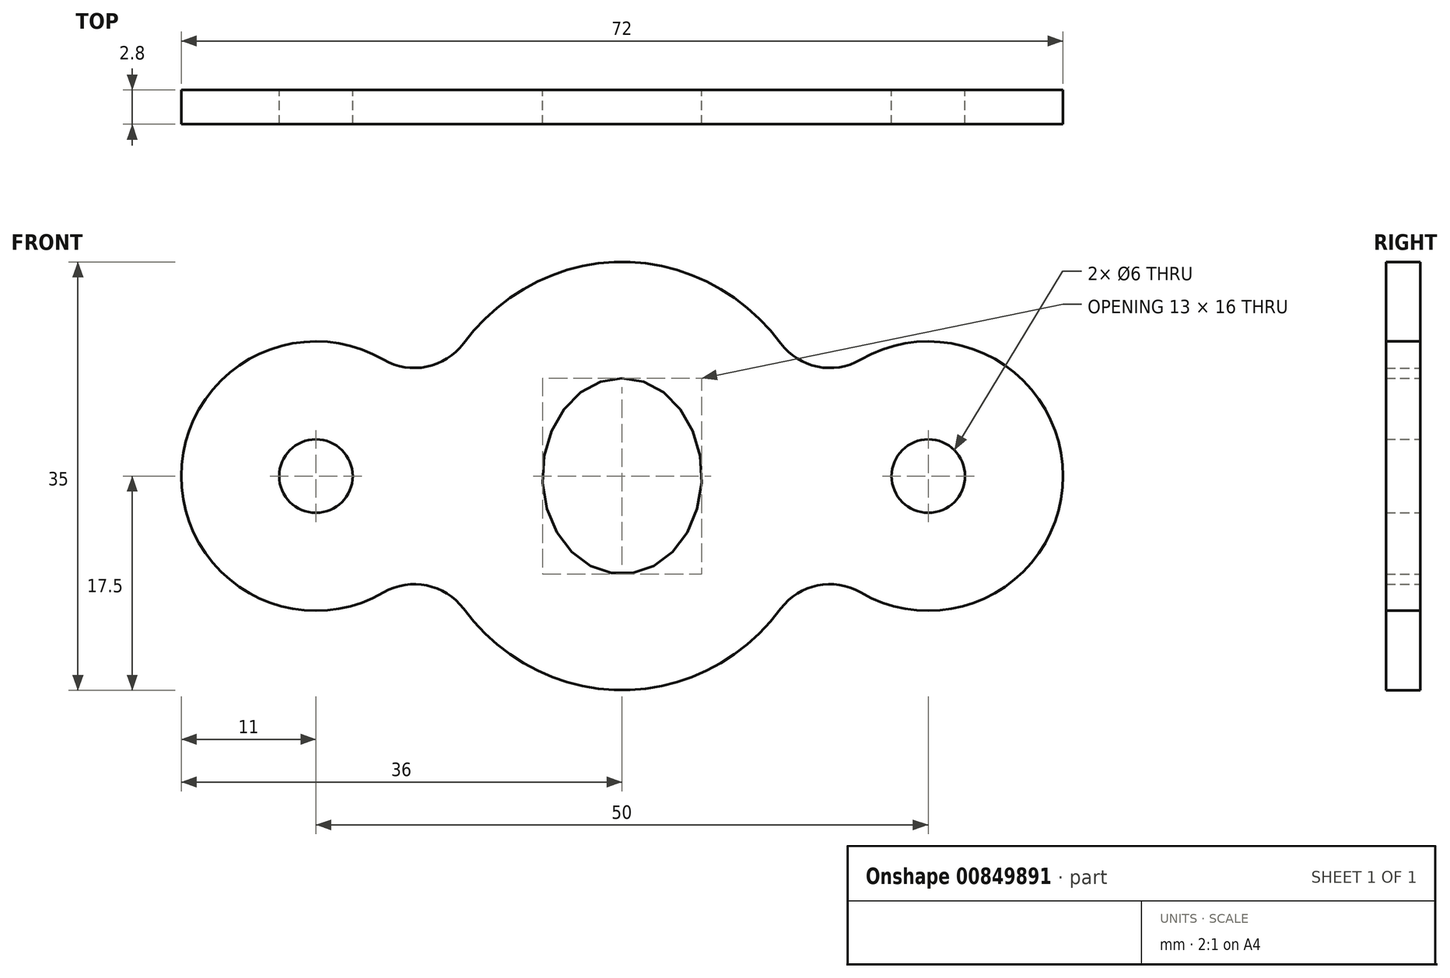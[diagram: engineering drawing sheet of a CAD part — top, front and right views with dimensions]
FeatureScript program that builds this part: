
annotation { "Feature Type Name" : "Feature", "Feature Type Description" : "" }
export const myFeature = defineFeature(function(context is Context, id is Id, definition is map)
    precondition{}
    {
        {
            var Q0;
            Q0=qCreatedBy(makeId("Front.planeOp"),FACE);
            var sketch = newSketch(context, id + "F0", { "sketchPlane" : qUnion([Q0])});
            skEllipse(sketch, "E0", {"center": v(0, 0) * mm, "majorRadius": 17.5 * mm, "minorRadius": 16.5 * mm, "majorAxis": v(0, 1)});
            skCircle(sketch, "E1", {"center": v(25, 0) * mm, "radius": 11 * mm});
            skCircle(sketch, "E2", {"center": v(-25, 0) * mm, "radius": 11 * mm});
            skCircle(sketch, "E3", {"center": v(-25, 0) * mm, "radius": 3 * mm});
            skCircle(sketch, "E4", {"center": v(25, 0) * mm, "radius": 3 * mm});
            skEllipse(sketch, "E5", {"center": v(0, 0) * mm, "majorRadius": 8 * mm, "minorRadius": 6.5 * mm, "majorAxis": v(0, 1)});
            skSolve(sketch);
        }
        {
            var Q0;
            Q0=qSketchRegion(id+"F0",true);
            extrude(context, id + "F1", {"entities" : qUnion([Q0]), "depth" : 2.8 * mm, "offsetDistance" : 25 * mm});
        }
        {
            var Q0;
            {var subQ0=sQuery(id+"F0.wireOp",EDGE,"E2");var subQ1=sQuery(id+"F0.wireOp",EDGE,"E0");Q0=makeQuery(id+"F1.opExtrude","SWEPT_EDGE",EDGE,{"disambiguationData":[OSD([subQ1,subQ0]),TDD([makeQuery(id+"F0.imprint","INTERSECT",VERTEX,{"disambiguationData":[OD(0.0)],"derivedFrom":[subQ1,subQ0]})])]});}
            var Q1;
            {var subQ0=sQuery(id+"F0.wireOp",EDGE,"E1");var subQ1=sQuery(id+"F0.wireOp",EDGE,"E0");Q1=makeQuery(id+"F1.opExtrude","SWEPT_EDGE",EDGE,{"disambiguationData":[OSD([subQ1,subQ0]),TDD([makeQuery(id+"F0.imprint","INTERSECT",VERTEX,{"disambiguationData":[OD(0.0)],"derivedFrom":[subQ1,subQ0]})])]});}
            var Q2;
            {var subQ0=sQuery(id+"F0.wireOp",EDGE,"E1");var subQ1=sQuery(id+"F0.wireOp",EDGE,"E0");Q2=makeQuery(id+"F1.opExtrude","SWEPT_EDGE",EDGE,{"disambiguationData":[OSD([subQ1,subQ0]),TDD([makeQuery(id+"F0.imprint","INTERSECT",VERTEX,{"disambiguationData":[OD(1.0)],"derivedFrom":[subQ1,subQ0]})])]});}
            var Q3;
            {var subQ0=sQuery(id+"F0.wireOp",EDGE,"E2");var subQ1=sQuery(id+"F0.wireOp",EDGE,"E0");Q3=makeQuery(id+"F1.opExtrude","SWEPT_EDGE",EDGE,{"disambiguationData":[OSD([subQ1,subQ0]),TDD([makeQuery(id+"F0.imprint","INTERSECT",VERTEX,{"disambiguationData":[OD(1.0)],"derivedFrom":[subQ1,subQ0]})])]});}
            fillet(context, id + "F2", {"entities" : qUnion([Q0, Q1, Q2, Q3]), "radius" : 5 * mm, "tangentPropagation" : true, "allowEdgeOverflow" : false});
        }
    });
